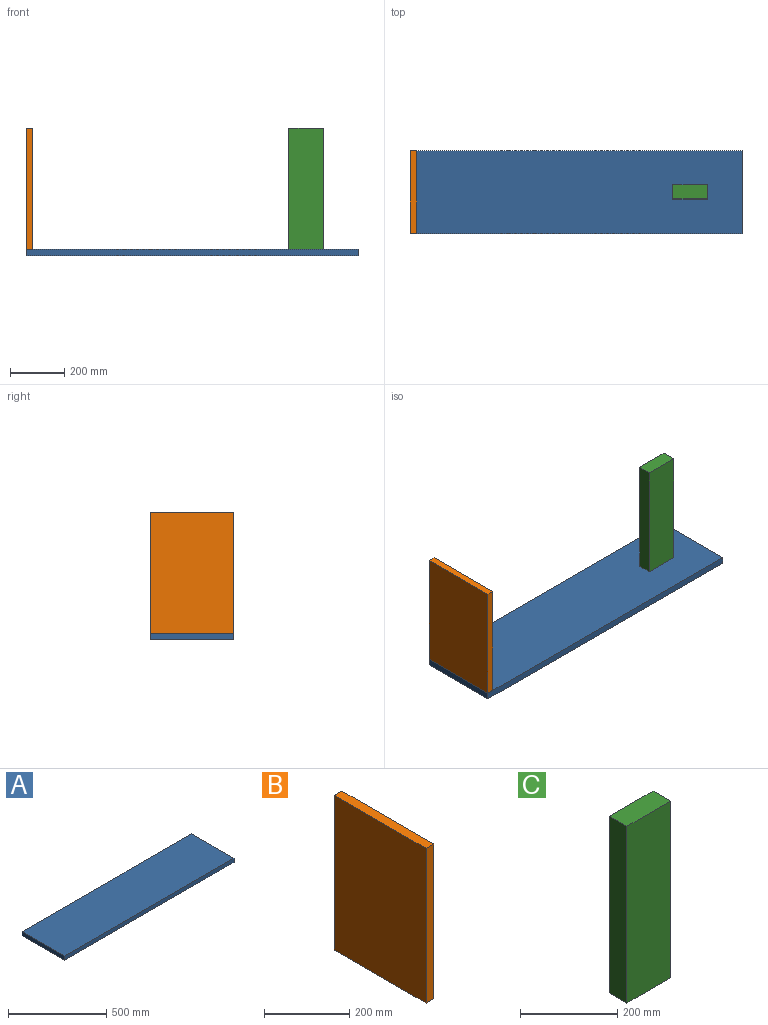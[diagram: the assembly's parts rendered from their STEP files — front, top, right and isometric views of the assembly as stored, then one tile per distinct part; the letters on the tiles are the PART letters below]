
ASSEMBLY  parts=3 mates=2
PART A: 6 faces, bbox 1219.2x304.8x25.4 mm
  f0: plane 304.8x25.4mm, normal (1,0,0), area 7741.9mm2, adj f1,f3,f4,f5
  f1: plane 1219.2x25.4mm, normal (0,1,0), area 30967.7mm2, adj f0,f2,f4,f5
  f2: plane 304.8x25.4mm, normal (-1,0,0), area 7741.9mm2, adj f1,f3,f4,f5
  f3: plane 1219.2x25.4mm, normal (0,-1,0), area 30967.7mm2, adj f0,f2,f4,f5
  f4: plane 1219.2x304.8mm, normal (0,0,1), area 371612.2mm2, adj f0,f1,f2,f3
  f5: plane 1219.2x304.8mm, normal (0,0,-1), area 371612.2mm2, adj f0,f1,f2,f3
PART B: 6 faces, bbox 25.4x304.8x444.5 mm
  f0: plane 304.8x25.4mm, normal (0,0,-1), area 7741.9mm2, adj f1,f3,f4,f5
  f1: plane 444.5x25.4mm, normal (0,1,0), area 11290.3mm2, adj f0,f2,f4,f5
  f2: plane 304.8x25.4mm, normal (0,0,1), area 7741.9mm2, adj f1,f3,f4,f5
  f3: plane 444.5x25.4mm, normal (0,-1,0), area 11290.3mm2, adj f0,f2,f4,f5
  f4: plane 444.5x304.8mm, normal (1,0,0), area 135483.6mm2, adj f0,f1,f2,f3
  f5: plane 444.5x304.8mm, normal (-1,0,0), area 135483.6mm2, adj f0,f1,f2,f3
PART C: 6 faces, bbox 127x50.8x444.5 mm
  f0: plane 127x50.8mm, normal (0,0,-1), area 6451.6mm2, adj f1,f3,f4,f5
  f1: plane 444.5x50.8mm, normal (1,0,0), area 22580.6mm2, adj f0,f2,f4,f5
  f2: plane 127x50.8mm, normal (0,0,1), area 6451.6mm2, adj f1,f3,f4,f5
  f3: plane 444.5x50.8mm, normal (-1,0,0), area 22580.6mm2, adj f0,f2,f4,f5
  f4: plane 444.5x127mm, normal (0,-1,0), area 56451.5mm2, adj f0,f1,f2,f3
  f5: plane 444.5x127mm, normal (0,1,0), area 56451.5mm2, adj f0,f1,f2,f3
PLACE A at identity fixed
PLACE B t=(-609.6,0,247.65)mm
PLACE C t=(419.1,25.4,247.65)mm
MATE fastened B.f0 <-> A.f4  axis (0,0,-1) through (-609.6,0,25.4)mm
MATE fastened C.f0 <-> A.f4  axis (0,0,-1) through (482.6,0,25.4)mm
